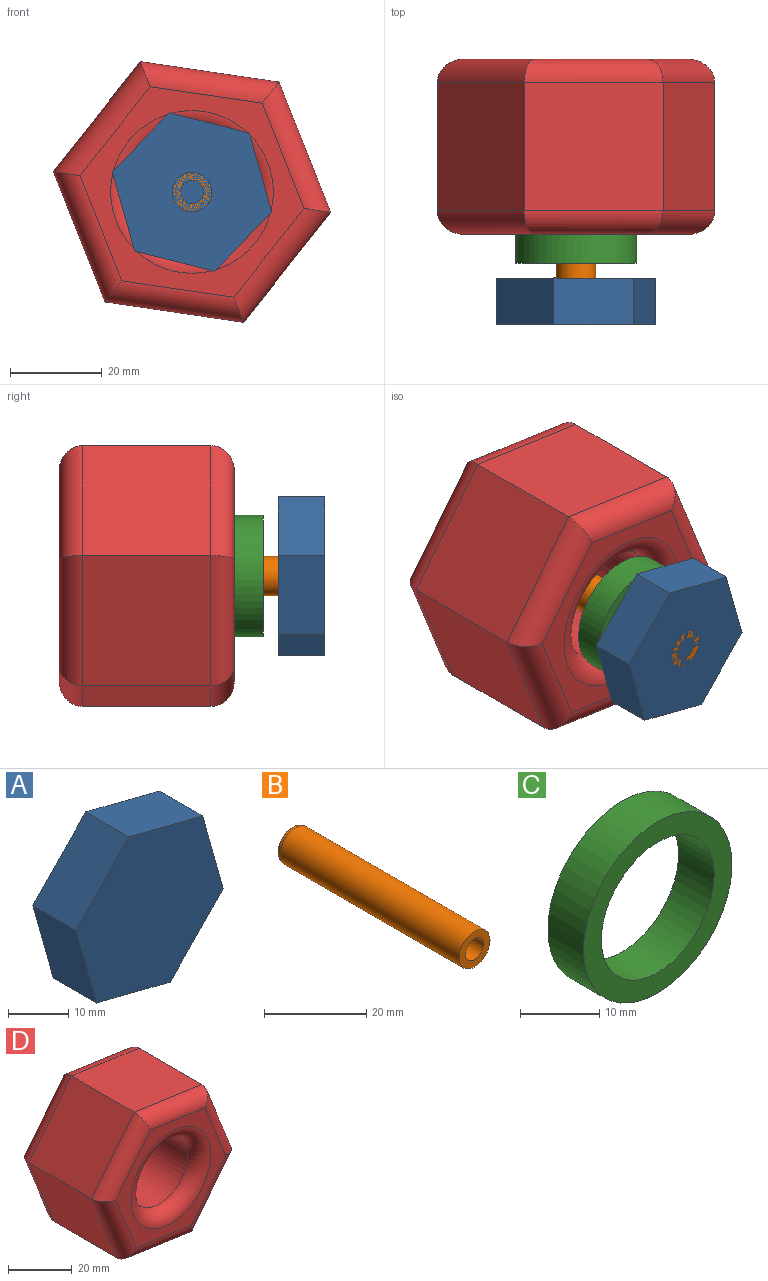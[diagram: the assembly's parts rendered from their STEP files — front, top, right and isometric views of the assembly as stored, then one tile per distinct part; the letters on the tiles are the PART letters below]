
ASSEMBLY  parts=4 mates=3
PART A: 8 faces, bbox 34.7x10.2x34.5 mm
  f0: plane 12.83x12.51mm, normal (-0.72,0,0.7), area 182mm2, adj f1,f5,f6,f7
  f1: plane 17.25x10.16mm, normal (-0.96,0,-0.27), area 182mm2, adj f0,f2,f6,f7
  f2: plane 17.36x10.16mm, normal (-0.25,0,-0.97), area 182mm2, adj f1,f3,f6,f7
  f3: plane 12.83x12.51mm, normal (0.72,0,-0.7), area 182mm2, adj f2,f4,f6,f7
  f4: plane 17.25x10.16mm, normal (0.96,0,0.27), area 182mm2, adj f3,f5,f6,f7
  f5: plane 17.36x10.16mm, normal (0.25,0,0.97), area 182mm2, adj f0,f4,f6,f7
  f6: plane 34.73x34.49mm, normal (0,-1,0), area 834.1mm2, adj f0,f1,f2,f3,f4,f5
  f7: plane 34.73x34.49mm, normal (0,1,0), area 834.1mm2, adj f0,f1,f2,f3,f4,f5
PART B: 5 faces, bbox 8.6x50.8x8.6 mm
  f0: cylinder r=2.51mm len=50.8mm, axis (0,-1,0), area 800.1mm2, adj f2,f3
  f1: cylinder r=4.28mm len=49.57mm, axis (0,-1,0), area 1333.6mm2, adj f3,f4
  f2: plane 6.12x6.12mm, normal (0,1,0), area 9.6mm2, adj f0,f4
  f3: plane 8.56x8.56mm, normal (0,-1,0), area 37.9mm2, adj f0,f1
  f4: bspline ~8.56x8.56mm, area 48.3mm2, adj f1,f2
PART C: 4 faces, bbox 26.4x6.4x26.4 mm
  f0: cylinder r=10.05mm len=20.11mm, axis (0,1,0), area 401.2mm2, adj f2,f3
  f1: cylinder r=13.22mm len=26.44mm, axis (0,1,0), area 527.4mm2, adj f2,f3
  f2: plane 26.44x26.44mm, normal (0,-1,0), area 231.4mm2, adj f0,f1
  f3: plane 26.44x26.44mm, normal (0,1,0), area 231.4mm2, adj f0,f1
PART D: 23 faces, bbox 60.4x38.1x56.7 mm
  f0: plane 28.37x27.94mm, normal (0.93,0,0.37), area 852.7mm2, adj f1,f6,f11,f18
  f1: plane 30.19x27.94mm, normal (0.15,0,0.99), area 852.7mm2, adj f0,f2,f10,f17
  f2: plane 27.94x23.93mm, normal (-0.78,0,0.62), area 852.7mm2, adj f1,f3,f12,f19
  f3: plane 28.37x27.94mm, normal (-0.93,0,-0.37), area 852.7mm2, adj f2,f4,f14,f21
  f4: plane 30.19x27.94mm, normal (-0.15,0,-0.99), area 852.7mm2, adj f3,f6,f15,f22
  f5: cylinder r=12.62mm len=27.94mm, axis (0,1,0), area 2215mm2, adj f9,f16
  f6: plane 27.94x23.93mm, normal (0.78,0,-0.62), area 852.7mm2, adj f0,f4,f13,f20
  f7: plane 48.78x45.83mm, normal (0,-1,0), area 595mm2, adj f16,f17,f18,f19,f20,f21,f22
  f8: plane 48.78x45.83mm, normal (0,1,0), area 595mm2, adj f9,f10,f11,f12,f13,f14,f15
  f9: torus R=17.7mm, axis (0,-1,0), area 725.2mm2, adj f5,f8
  f10: cylinder r=5.08mm len=30.93mm, axis (-0.99,0,0.15), area 226.5mm2, adj f1,f8,f11,f12
  f11: cylinder r=5.08mm len=30.24mm, axis (-0.37,0,0.93), area 226.5mm2, adj f0,f8,f10,f13
  f12: cylinder r=5.08mm len=27.08mm, axis (-0.62,0,-0.78), area 226.5mm2, adj f2,f8,f10,f14
  f13: cylinder r=5.08mm len=27.08mm, axis (0.62,0,0.78), area 226.5mm2, adj f6,f8,f11,f15
  f14: cylinder r=5.08mm len=30.24mm, axis (0.37,0,-0.93), area 226.5mm2, adj f3,f8,f12,f15
  f15: cylinder r=5.08mm len=30.93mm, axis (0.99,0,-0.15), area 226.5mm2, adj f4,f8,f13,f14
  f16: torus R=17.7mm, axis (0,-1,0), area 725.2mm2, adj f5,f7
  f17: cylinder r=5.08mm len=30.93mm, axis (0.99,0,-0.15), area 226.5mm2, adj f1,f7,f18,f19
  f18: cylinder r=5.08mm len=30.24mm, axis (0.37,0,-0.93), area 226.5mm2, adj f0,f7,f17,f20
  f19: cylinder r=5.08mm len=27.08mm, axis (0.62,0,0.78), area 226.5mm2, adj f2,f7,f17,f21
  f20: cylinder r=5.08mm len=27.08mm, axis (-0.62,0,-0.78), area 226.5mm2, adj f6,f7,f18,f22
  f21: cylinder r=5.08mm len=30.24mm, axis (-0.37,0,0.93), area 226.5mm2, adj f3,f7,f19,f22
  f22: cylinder r=5.08mm len=30.93mm, axis (-0.99,0,0.15), area 226.5mm2, adj f4,f7,f20,f21
PLACE A t=(69.58,-47.65,7.44)mm
PLACE B t=(69.58,-57.81,7.44)mm
PLACE C t=(69.65,-38.1,7.2)mm
PLACE D at identity
MATE parallel A.f6 <-> B.f0  axis (0,-1,0) through (32.81,-57.81,28.2)mm
MATE cylindrical C.f0 <-> D.f5  axis (0,1,0) through (32.81,-38.1,28.2)mm
MATE pin_slot B.f0 <-> D.f5  axis (0,-1,0) through (32.81,-33.02,28.2)mm
